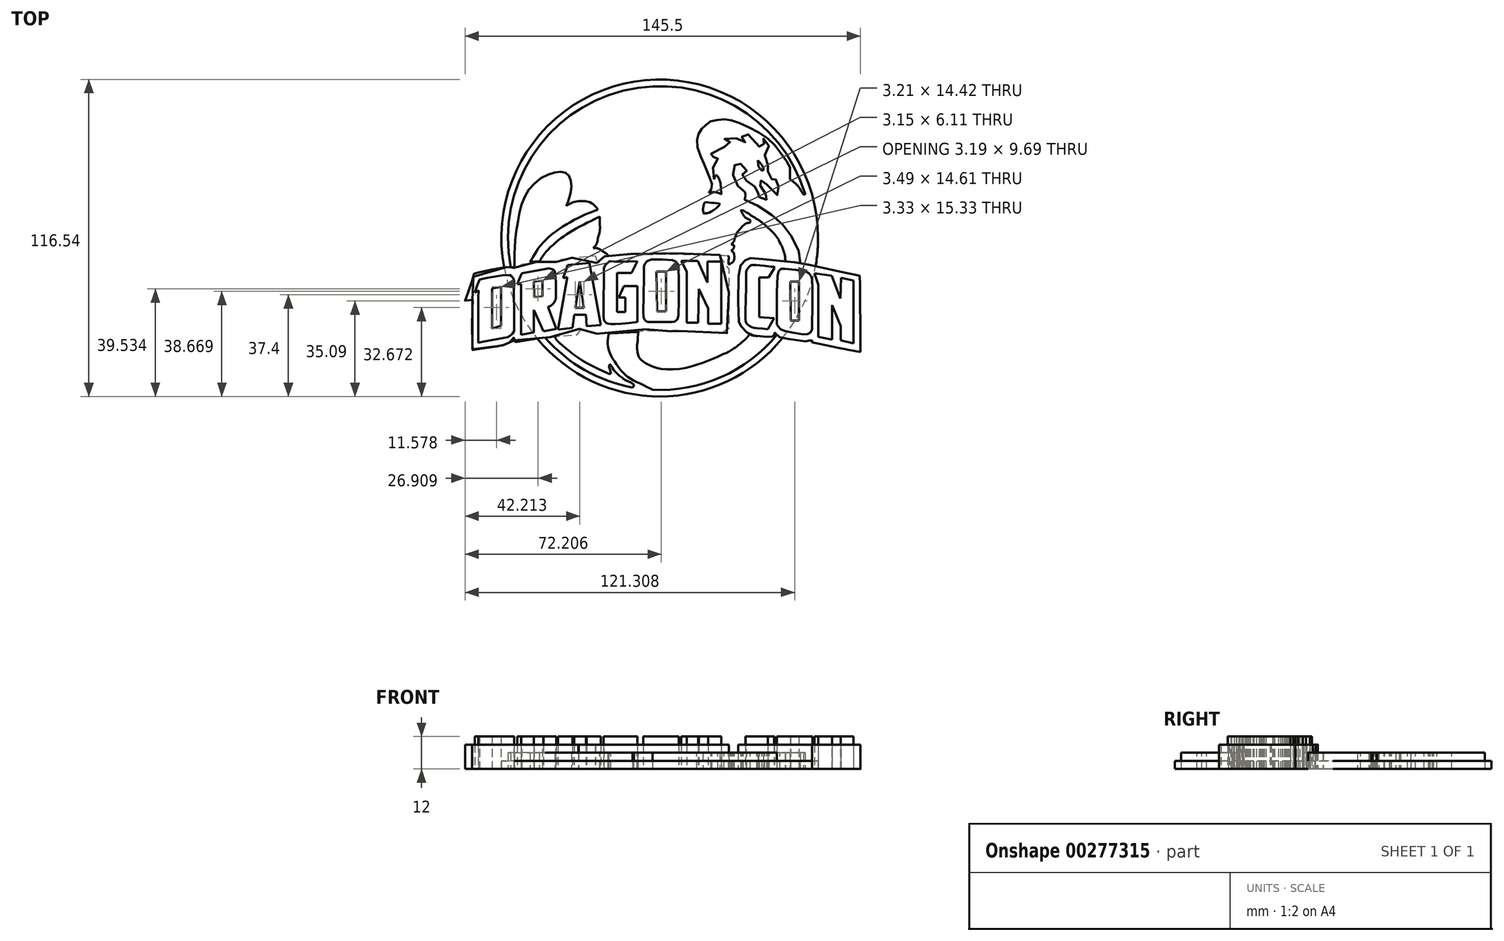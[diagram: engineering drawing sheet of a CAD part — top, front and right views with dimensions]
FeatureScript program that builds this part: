
annotation { "Feature Type Name" : "Feature", "Feature Type Description" : "" }
export const myFeature = defineFeature(function(context is Context, id is Id, definition is map)
    precondition{}
    {
        {
            var Q0;
            Q0=qCreatedBy(makeId("Top.planeOp"),FACE);
            var sketch = newSketch(context, id + "F0", { "sketchPlane" : qUnion([Q0])});
            skCircle(sketch, "E0", {"center": v(-3.25, 16.34) * mm, "radius": 58.27 * mm});
            skCircle(sketch, "E1.0", {"center": v(-3.25, 16.34) * mm, "radius": 55.87 * mm});
            skFitSpline(sketch, "E2", {"points": [v(-50.97, 7.43) * mm, v(-47.94, 12.58) * mm, v(-41.78, 18.63) * mm, v(-32.6, 24.12) * mm, v(-26.1, 26.81) * mm], "startDerivative": vector(12.2, 23.84) * mm, "endDerivative": vector(26.36, 9.93) * mm});
            skFitSpline(sketch, "E3", {"points": [v(-37.64, 28.16) * mm, v(-35.28, 29.5) * mm, v(-32.03, 29.95) * mm, v(-29, 29.5) * mm, v(-26.88, 27.93) * mm, v(-26.1, 26.81) * mm], "startDerivative": vector(10.69, 7.53) * mm, "endDerivative": vector(4.39, -7.37) * mm});
            skFitSpline(sketch, "E4", {"points": [v(-56.8, 5.63) * mm, v(-56.68, 10.34) * mm, v(-56.57, 14.49) * mm, v(-55.45, 22.55) * mm, v(-53.77, 29.61) * mm, v(-50.09, 35.78) * mm, v(-44.47, 39.7) * mm, v(-40.32, 40.7) * mm, v(-37.75, 40.26) * mm, v(-36.3, 38.47) * mm, v(-35.84, 35.78) * mm, v(-36.18, 32.42) * mm, v(-36.96, 30.06) * mm, v(-37.64, 28.16) * mm], "startDerivative": vector(1.87, 60.35) * mm, "endDerivative": vector(-12.09, -35.42) * mm});
            skFitSpline(sketch, "E5", {"points": [v(-25.35, 24.17) * mm, v(-30.1, 21.94) * mm, v(-36.47, 18.42) * mm, v(-40.6, 15.5) * mm, v(-44.44, 12.05) * mm, v(-46.28, 9.75) * mm, v(-47.58, 7.76) * mm], "startDerivative": vector(-25.1, -11.24) * mm, "endDerivative": vector(-10.5, -16.52) * mm});
            skFitSpline(sketch, "E6", {"points": [v(-27.73, 12.67) * mm, v(-26.5, 14.35) * mm, v(-26.04, 16.2) * mm, v(-25.35, 19.1) * mm, v(-25.35, 21.94) * mm, v(-25.35, 24.17) * mm], "startDerivative": vector(7.73, 8.84) * mm, "endDerivative": vector(0.24, 11.19) * mm});
            skFitSpline(sketch, "E7", {"points": [v(-27.73, 12.67) * mm, v(-26.5, 12.67) * mm, v(-24.9, 11.9) * mm, v(-22.6, 10.37) * mm], "startDerivative": vector(4.49, 0.5) * mm, "endDerivative": vector(5.86, -4.02) * mm});
            skFitSpline(sketch, "E8", {"points": [v(19.1, 32.6) * mm, v(17.27, 33.21) * mm, v(14.74, 32.9) * mm], "startDerivative": vector(-3.76, 1.76) * mm, "endDerivative": vector(-4.95, -1.08) * mm});
            skFitSpline(sketch, "E9", {"points": [v(49.54, 32.52) * mm, v(48.62, 33.9) * mm, v(47.62, 35.43) * mm, v(46.32, 36.66) * mm, v(44.63, 37.96) * mm], "startDerivative": vector(-3.93, 5.66) * mm, "endDerivative": vector(-6.46, 4.91) * mm});
            skFitSpline(sketch, "E10", {"points": [v(44.63, 42.4) * mm, v(44.63, 41.03) * mm, v(44.63, 37.96) * mm], "startDerivative": vector(0, -3.1) * mm, "endDerivative": vector(0, -5.62) * mm});
            skFitSpline(sketch, "E11", {"points": [v(44.63, 42.4) * mm, v(43.07, 44.98) * mm, v(39.76, 49.62) * mm, v(35.83, 53.38) * mm, v(29.87, 56.9) * mm, v(24.29, 59.37) * mm, v(21.2, 59.97) * mm, v(18.51, 59.86) * mm, v(15.62, 59.32) * mm, v(14.02, 58.24) * mm, v(12.5, 56.88) * mm, v(11.2, 55.01) * mm, v(10.63, 53.36) * mm, v(10.38, 50.92) * mm, v(12.12, 45.66) * mm, v(13.4, 42.76) * mm, v(14.77, 39.1) * mm, v(15.62, 37.18) * mm, v(15.91, 35) * mm, v(15.29, 33.84) * mm, v(14.74, 32.9) * mm], "startDerivative": vector(-28.1, 47.85) * mm, "endDerivative": vector(-17.14, -31.73) * mm});
            skFitSpline(sketch, "E12", {"points": [v(16.7, 37.9) * mm, v(16.86, 38.65) * mm, v(17.05, 39.17) * mm, v(17.29, 39.37) * mm, v(17.5, 39.43) * mm, v(17.78, 39.35) * mm, v(18.01, 39.03) * mm, v(18.43, 38.29) * mm, v(18.72, 37.72) * mm, v(18.8, 37.47) * mm, v(18.86, 37.1) * mm, v(19.1, 36.26) * mm, v(19.32, 33.08) * mm, v(19.39, 32.6) * mm, v(19.1, 32.6) * mm], "startDerivative": vector(1.88, 9.22) * mm, "endDerivative": vector(-7.19, 1.13) * mm});
            skFitSpline(sketch, "E13", {"points": [v(16.7, 37.9) * mm, v(16.28, 37.9) * mm, v(16.04, 38.79) * mm, v(16.02, 41.8) * mm, v(16.7, 42.73) * mm, v(17.34, 43.42) * mm, v(17.94, 44.76) * mm, v(18.1, 45.34) * mm, v(18.07, 45.8) * mm, v(17.88, 46.28) * mm, v(17.58, 46.58) * mm, v(17.13, 46.6) * mm, v(16.7, 46.5) * mm, v(16.4, 46.18) * mm, v(16.34, 45.57) * mm, v(16, 45.2) * mm, v(15.63, 45.57) * mm, v(15.53, 46.95) * mm, v(15.73, 47.56) * mm, v(18.35, 49.77) * mm, v(18.72, 49.83) * mm, v(21.74, 49.93) * mm, v(22.19, 50.08) * mm, v(22.57, 50.42) * mm, v(22.63, 50.87) * mm, v(22.57, 51.35) * mm, v(22.4, 51.86) * mm, v(21.84, 52.15) * mm, v(20.89, 52.09) * mm, v(20.56, 52.13) * mm, v(20.4, 52.43) * mm, v(20.62, 52.88) * mm, v(21.64, 53.14) * mm, v(23.35, 53.34) * mm, v(24.62, 53.16) * mm, v(25.33, 52.63) * mm, v(26.19, 51.92) * mm, v(27.39, 51.54) * mm, v(28.2, 51.66) * mm, v(28.58, 52.27) * mm, v(28.52, 53.1) * mm, v(28.01, 53.45) * mm, v(27.02, 53.45) * mm, v(26.76, 53.65) * mm, v(26.8, 54) * mm, v(27.06, 54.32) * mm, v(27.77, 54.52) * mm, v(29.11, 54.48) * mm, v(29.84, 54.26) * mm, v(32.75, 50.58) * mm, v(33.3, 50) * mm, v(33.76, 49.9) * mm, v(34.09, 49.91) * mm, v(34.47, 50.01) * mm, v(34.8, 50.26) * mm, v(35.06, 50.58) * mm, v(35.08, 51) * mm, v(35, 51.42) * mm, v(34.63, 51.66) * mm, v(34.37, 51.98) * mm, v(34.29, 52.33) * mm, v(34.37, 52.71) * mm, v(34.84, 52.88) * mm, v(35.4, 52.65) * mm, v(36.01, 52.1) * mm, v(36.32, 51.62) * mm, v(36.7, 50.93) * mm, v(36.77, 49.04) * mm, v(36.48, 48.35) * mm, v(36.08, 47.64) * mm, v(35.38, 46.97) * mm, v(35.34, 46.75) * mm, v(35.36, 46.26) * mm, v(35.34, 45.22) * mm, v(35.87, 44.15) * mm, v(36.8, 42.77) * mm, v(36.93, 42.38) * mm, v(36.85, 41.77) * mm, v(36.56, 41.6) * mm, v(36.48, 41.3) * mm, v(36.44, 40.92) * mm, v(36.48, 40.37) * mm, v(36.48, 39.84) * mm, v(36.79, 39.3) * mm, v(37.35, 38.64) * mm, v(38.09, 37.75) * mm, v(38.51, 37.28) * mm, v(38.73, 37.18) * mm, v(39.06, 37.22) * mm, v(39.16, 37.37) * mm, v(39.2, 37.59) * mm, v(39.26, 37.73) * mm, v(39.55, 37.9) * mm, v(39.8, 37.71) * mm, v(39.91, 37.26) * mm, v(40.16, 35.82) * mm, v(40.28, 35.11) * mm, v(40.52, 35.42) * mm, v(40.95, 31.01) * mm, v(40.85, 30.97) * mm, v(39.06, 33.35) * mm, v(37.31, 35.07) * mm, v(36.12, 36.05) * mm, v(36.1, 36.07) * mm, v(36.12, 36.07) * mm, v(36.48, 36.35) * mm], "startDerivative": vector(-64.1, -13.42) * mm, "endDerivative": vector(60.5, 53.27) * mm});
            skFitSpline(sketch, "E14", {"points": [v(36.12, 36.07) * mm, v(35.12, 37.15) * mm, v(34.57, 37.47) * mm, v(34.18, 37.57) * mm, v(33.81, 37.46) * mm, v(33.6, 37.13) * mm, v(33.5, 36.78) * mm, v(33.53, 36.18) * mm, v(33.72, 35.5) * mm, v(34.37, 34.3) * mm, v(35.57, 32.65) * mm, v(36.12, 31.8) * mm, v(36.26, 30.98) * mm, v(36.22, 30.43) * mm, v(35.73, 30.61) * mm, v(34.7, 31.2) * mm, v(33.99, 31.42) * mm, v(32.9, 31.45) * mm, v(32.44, 31.7) * mm, v(32.63, 32.04) * mm, v(32.87, 32.46) * mm, v(32.96, 32.86) * mm, v(32.91, 33.13) * mm, v(32.7, 33.78) * mm, v(32.03, 34.83) * mm, v(31.1, 35.85) * mm, v(29.88, 36.62) * mm, v(28.5, 37.5) * mm, v(27.5, 38.23) * mm, v(27.08, 38.9) * mm, v(27.11, 39.74) * mm, v(27.57, 40.34) * mm, v(28.4, 40.66) * mm, v(28.63, 40.75) * mm, v(28.66, 41.17) * mm, v(28.4, 41.74) * mm, v(26.94, 43.34) * mm, v(26.27, 43.7) * mm, v(25.45, 43.76) * mm, v(24.66, 43.62) * mm, v(24.34, 43.27) * mm, v(23.87, 42.1) * mm, v(23.7, 40.75) * mm, v(23.8, 39.02) * mm, v(24.66, 36.86) * mm, v(25.92, 34.99) * mm, v(27.23, 33.75) * mm, v(27.88, 33.28) * mm, v(28.47, 33.04) * mm, v(28.78, 32.38) * mm, v(28.66, 31.99) * mm, v(28.3, 31.88) * mm, v(27.97, 32.28) * mm, v(27.44, 31.94) * mm, v(27.52, 30.77) * mm, v(27.96, 30.48) * mm, v(30.2, 29.65) * mm, v(33.98, 27.55) * mm, v(37.62, 25.05) * mm, v(40.25, 22.92) * mm, v(42.51, 20.58) * mm, v(44.37, 18.12) * mm, v(45.9, 15.85) * mm, v(47.92, 11.49) * mm, v(48.4, 8.13) * mm, v(48.36, 7.2) * mm], "startDerivative": vector(-57.86, 70.9) * mm, "endDerivative": vector(-4.92, -56.1) * mm});
            skFitSpline(sketch, "E15", {"points": [v(13.27, 29.46) * mm, v(12.95, 28.76) * mm, v(12.7, 27.87) * mm, v(12.62, 26.9) * mm, v(12.66, 26.06) * mm, v(12.9, 25.4) * mm, v(13.04, 25.35) * mm, v(13.53, 25.43) * mm, v(14.79, 25.7) * mm, v(16.58, 26.68) * mm, v(18.8, 28.76) * mm, v(18.74, 29) * mm, v(16.54, 29.26) * mm, v(14.72, 29.42) * mm, v(13.27, 29.46) * mm]});
            skFitSpline(sketch, "E16", {"points": [v(26.9, 26.8) * mm, v(28.62, 25.8) * mm, v(30.72, 24.44) * mm, v(33.66, 22.55) * mm, v(36.65, 20.04) * mm, v(38.21, 18.56) * mm, v(38.95, 17.71) * mm, v(40.1, 16.25) * mm, v(40.7, 15.15) * mm, v(41.43, 13.7) * mm, v(41.82, 12.95) * mm, v(42.23, 11.73) * mm, v(42.69, 10.09) * mm, v(42.92, 8.04) * mm], "startDerivative": vector(21.56, -12.1) * mm, "endDerivative": vector(1.9, -26.3) * mm});
            skFitSpline(sketch, "E17", {"points": [v(26.83, 26.8) * mm, v(26.62, 26.7) * mm, v(26.85, 25.9) * mm, v(27.63, 24.56) * mm, v(28.04, 24.07) * mm, v(28.83, 23.49) * mm, v(29.65, 23.14) * mm, v(29.95, 22.88) * mm, v(30, 22.5) * mm, v(29.95, 22.1) * mm, v(29.16, 21.92) * mm, v(28.38, 21.72) * mm, v(27.52, 21.01) * mm, v(26.64, 20.2) * mm, v(25.78, 19.14) * mm, v(25.3, 18.58) * mm, v(24.77, 17.5) * mm, v(24.3, 16.2) * mm, v(24.06, 15.38) * mm, v(23.52, 14.54) * mm, v(23.15, 14.13) * mm, v(23.33, 13.9) * mm, v(23.67, 13.85) * mm, v(24, 13.66) * mm, v(24.06, 13.14) * mm, v(23.82, 12.47) * mm, v(23.28, 12.04) * mm, v(23.18, 11.5) * mm, v(23.76, 11.2) * mm, v(24.1, 9.87) * mm, v(24.06, 8.45) * mm, v(23.9, 7.91) * mm, v(23.71, 7.63) * mm, v(22.79, 6.97) * mm, v(22.34, 6.77) * mm], "startDerivative": vector(-16.2, -3.25) * mm, "endDerivative": vector(-16.34, -5.45) * mm});
            skFitSpline(sketch, "E18", {"points": [v(-40.23, -22.15) * mm, v(-38.16, -23.95) * mm, v(-35.75, -25.9) * mm, v(-32.9, -27.94) * mm, v(-29.2, -30.12) * mm, v(-24.86, -32.23) * mm, v(-22.72, -33.26) * mm, v(-21.49, -33.68) * mm, v(-21.3, -33.5) * mm, v(-21.34, -33.19) * mm, v(-21.49, -32.69) * mm, v(-21.68, -31.77) * mm, v(-21.83, -31.39) * mm, v(-21.91, -30.24) * mm, v(-21.57, -30.16) * mm, v(-21.18, -30.5) * mm, v(-20.76, -31.35) * mm, v(-20, -32.42) * mm, v(-18.88, -33.65) * mm, v(-17.04, -35.1) * mm], "startDerivative": vector(28.15, -24.84) * mm, "endDerivative": vector(29.6, -21.78) * mm});
            skFitSpline(sketch, "E19", {"points": [v(-17.04, -35.1) * mm, v(-15.55, -36.1) * mm, v(-13.75, -36.9) * mm, v(-12.9, -37.48) * mm, v(-12.79, -37.86) * mm, v(-13.33, -38.6) * mm], "startDerivative": vector(5.46, -4.1) * mm, "endDerivative": vector(-4.14, -3) * mm});
            skFitSpline(sketch, "E20", {"points": [v(32.76, 44.92) * mm, v(33.4, 44.27) * mm, v(34.36, 43.1) * mm, v(34.8, 42.23) * mm, v(34.8, 42.1) * mm, v(34.8, 41.34) * mm, v(34.66, 41.25) * mm, v(34.43, 41.23) * mm, v(34.14, 41.3) * mm, v(33.04, 42.68) * mm, v(33.02, 42.91) * mm, v(32.76, 44.92) * mm]});
            skFitSpline(sketch, "E21", {"points": [v(-11.42, -20.07) * mm, v(-11.47, -21.62) * mm, v(-11.68, -23.04) * mm, v(-11.64, -23.98) * mm, v(-11.52, -25.28) * mm, v(-11.28, -26.4) * mm, v(-11.12, -27.03) * mm, v(-10.98, -27.36) * mm, v(-10.6, -28) * mm, v(-10.03, -28.59) * mm, v(-9.33, -29.13) * mm, v(-8.28, -29.78) * mm, v(-6.81, -30.56) * mm, v(-5.08, -31.25) * mm, v(-3.09, -31.74) * mm, v(-0.2, -31.95) * mm, v(4, -31.77) * mm, v(7.46, -31.09) * mm, v(10.42, -30.2) * mm, v(15.41, -28.43) * mm, v(20, -26.37) * mm], "startDerivative": vector(0.6, -33.32) * mm, "endDerivative": vector(52.9, 25.28) * mm});
            skFitSpline(sketch, "E22", {"points": [v(20, -26.37) * mm, v(22.61, -25.17) * mm, v(25.76, -22.93) * mm, v(28.22, -20.87) * mm], "startDerivative": vector(8.27, 3.24) * mm, "endDerivative": vector(7.15, 6.13) * mm});
            skFitSpline(sketch, "E23", {"points": [v(-22.32, -20.3) * mm, v(-22.38, -23.47) * mm, v(-21.42, -26.48) * mm, v(-19.58, -29.61) * mm, v(-17.77, -32.06) * mm, v(-16.05, -33.9) * mm, v(-13.52, -35.7) * mm, v(-9.27, -37.72) * mm, v(-5.94, -39.46) * mm], "startDerivative": vector(-2.32, -26.36) * mm, "endDerivative": vector(24.45, -10.25) * mm});
            skFitSpline(sketch, "E24", {"points": [v(-69.99, -3.2) * mm, v(-69.95, -22.17) * mm], "startDerivative": vector(0.04, -18.97) * mm, "endDerivative": vector(0.04, -18.97) * mm});
            skFitSpline(sketch, "E25", {"points": [v(-69.95, -22.17) * mm, v(-59.54, -20.12) * mm, v(-58.9, -19.93) * mm, v(-58.38, -19.6) * mm, v(-57.8, -19.15) * mm, v(-57.22, -18.41) * mm, v(-56.87, -17.67) * mm, v(-56.87, -15.7) * mm, v(-56.95, 0.96) * mm, v(-57.15, 1.64) * mm, v(-57.48, 2) * mm, v(-58.14, 2.54) * mm, v(-58.59, 2.83) * mm, v(-58.77, 2.85) * mm, v(-69.3, 1.14) * mm, v(-69.43, 1.1) * mm, v(-71.42, -3.5) * mm, v(-71.32, -3.64) * mm, v(-71, -3.64) * mm, v(-69.99, -3.2) * mm], "startDerivative": vector(102.59, 19.96) * mm, "endDerivative": vector(26.52, 13.63) * mm});
            skFitSpline(sketch, "E26", {"points": [v(-65, -2.3) * mm, v(-65.03, -16.9) * mm], "startDerivative": vector(-0.04, -14.6) * mm, "endDerivative": vector(-0.04, -14.6) * mm});
            skFitSpline(sketch, "E27", {"points": [v(-61.77, -1.6) * mm, v(-65, -2.3) * mm], "startDerivative": vector(-3.22, -0.69) * mm, "endDerivative": vector(-3.22, -0.69) * mm});
            skFitSpline(sketch, "E28", {"points": [v(-61.83, -15.89) * mm, v(-61.77, -1.6) * mm], "startDerivative": vector(0.05, 14.28) * mm, "endDerivative": vector(0.05, 14.28) * mm});
            skFitSpline(sketch, "E29", {"points": [v(-65.03, -16.9) * mm, v(-61.83, -15.89) * mm], "startDerivative": vector(3.2, 1.01) * mm, "endDerivative": vector(3.2, 1.01) * mm});
            skFitSpline(sketch, "E30", {"points": [v(-46.45, 0.98) * mm, v(-49.44, 0.67) * mm], "startDerivative": vector(-3, -0.3) * mm, "endDerivative": vector(-3, -0.3) * mm});
            skFitSpline(sketch, "E31", {"points": [v(-46.3, -5.24) * mm, v(-46.45, 0.98) * mm], "startDerivative": vector(-0.14, 6.21) * mm, "endDerivative": vector(-0.14, 6.21) * mm});
            skFitSpline(sketch, "E32", {"points": [v(-49.52, -5.5) * mm, v(-46.3, -5.24) * mm], "startDerivative": vector(3.22, 0.26) * mm, "endDerivative": vector(3.22, 0.26) * mm});
            skFitSpline(sketch, "E33", {"points": [v(-49.44, 0.67) * mm, v(-49.52, -5.5) * mm], "startDerivative": vector(-0.08, -6.17) * mm, "endDerivative": vector(-0.08, -6.17) * mm});
            skFitSpline(sketch, "E34", {"points": [v(-22.6, 10.37) * mm, v(-22.15, 9.89) * mm, v(-20.92, 9.98) * mm, v(11.44, 10.37) * mm, v(21.6, 9.89) * mm], "startDerivative": vector(5.82, -7.96) * mm, "endDerivative": vector(24.52, -1.9) * mm});
            skFitSpline(sketch, "E35", {"points": [v(22.34, 6.77) * mm, v(22, 6.77) * mm, v(22.03, 9.66) * mm, v(21.6, 9.89) * mm], "startDerivative": vector(-2.05, -0.95) * mm, "endDerivative": vector(-2.24, -0.03) * mm});
            skFitSpline(sketch, "E36", {"points": [v(-50.97, 7.43) * mm, v(-49.6, 7.64) * mm, v(-47.58, 7.76) * mm], "startDerivative": vector(2.87, 0.5) * mm, "endDerivative": vector(3.87, 0.17) * mm});
            skFitSpline(sketch, "E37", {"points": [v(-56.8, 5.63) * mm, v(-56.8, 5.3) * mm], "startDerivative": vector(0, -0.34) * mm, "endDerivative": vector(0, -0.34) * mm});
            skFitSpline(sketch, "E38", {"points": [v(-56.8, 5.3) * mm, v(-57.15, 5.47) * mm, v(-57.59, 5.63) * mm, v(-58.08, 5.66) * mm], "startDerivative": vector(-1.09, 0.57) * mm, "endDerivative": vector(-1.42, 0.01) * mm});
            skFitSpline(sketch, "E39", {"points": [v(49.54, 32.52) * mm, v(49.83, 32.32) * mm, v(50.2, 32.6) * mm], "startDerivative": vector(0.62, -0.63) * mm, "endDerivative": vector(0.63, 0.75) * mm});
            skFitSpline(sketch, "E40", {"points": [v(42.92, 8.04) * mm, v(42.92, 7.69) * mm, v(43.04, 7.69) * mm, v(45.94, 7.43) * mm, v(48.35, 7.07) * mm, v(48.36, 7.07) * mm, v(48.36, 7.2) * mm], "startDerivative": vector(-0.35, -3.72) * mm, "endDerivative": vector(-0.1, 2.41) * mm});
            skFitSpline(sketch, "E41", {"points": [v(-56.8, 5.3) * mm, v(-56.33, 5.3) * mm, v(-56.12, 6.27) * mm, v(-55.26, 6.54) * mm, v(-50.97, 7.43) * mm], "startDerivative": vector(3.85, -1.21) * mm, "endDerivative": vector(11.27, 2.66) * mm});
            skFitSpline(sketch, "E42", {"points": [v(-47.58, 7.76) * mm, v(-45.09, 7.96) * mm, v(-43.55, 8.04) * mm, v(-42.59, 8.01) * mm, v(-41.8, 7.88) * mm, v(-41.22, 7.52) * mm, v(-40.23, 6.59) * mm, v(-39.98, 6.36) * mm, v(-39.94, 6.37) * mm, v(-39.04, 8.7) * mm, v(-38.98, 8.77) * mm, v(-26.98, 9.8) * mm, v(-26.98, 9.78) * mm, v(-26.55, 7.35) * mm, v(-26.36, 6.71) * mm, v(-26.2, 6.71) * mm, v(-25.77, 7.5) * mm, v(-25.11, 8.42) * mm, v(-24.31, 9.17) * mm, v(-23.42, 9.8) * mm, v(-22.6, 10.37) * mm], "startDerivative": vector(34.56, 2.98) * mm, "endDerivative": vector(17.1, 11.49) * mm});
            skFitSpline(sketch, "E43", {"points": [v(48.36, 7.07) * mm, v(49.74, 6.82) * mm, v(51.72, 6.34) * mm], "startDerivative": vector(2.9, -0.46) * mm, "endDerivative": vector(3.76, -0.96) * mm});
            skFitSpline(sketch, "E44", {"points": [v(22.2, 6.71) * mm, v(22.2, -17.98) * mm, v(22.2, -18.17) * mm, v(21.95, -18.45) * mm, v(21.05, -18.54) * mm, v(4.01, -17.8) * mm, v(3.69, -17.76) * mm, v(3.64, -17.6) * mm, v(3.64, -16.86) * mm, v(3.56, -16.9) * mm, v(3.3, -17.13) * mm, v(2.87, -17.5) * mm, v(2.32, -17.7) * mm, v(1.77, -17.9) * mm, v(0.3, -17.9) * mm, v(-7.27, -17.88) * mm, v(-7.61, -17.7) * mm, v(-8.37, -17.09) * mm, v(-8.48, -17.3) * mm, v(-8.75, -17.8) * mm, v(-8.94, -17.9) * mm, v(-32.16, -19.1) * mm, v(-32.38, -18.95) * mm, v(-32.73, -16.45) * mm, v(-33.22, -19.08) * mm, v(-33.43, -19.19) * mm, v(-37.87, -19.52) * mm, v(-45.42, -20.3) * mm], "startDerivative": vector(-1.58, -264.35) * mm, "endDerivative": vector(-101.85, -10.87) * mm});
            skFitSpline(sketch, "E45", {"points": [v(42.92, 7.69) * mm, v(41.83, 7.89) * mm, v(39.32, 8.26) * mm, v(36.49, 8.63) * mm, v(32.1, 9.18) * mm, v(29.87, 9.29) * mm, v(28.6, 8.84) * mm, v(27.32, 7.97) * mm, v(26.11, 6.42) * mm, v(25.76, 5.79) * mm, v(25.58, 4.23) * mm, v(25.51, -13.86) * mm, v(25.51, -14.02) * mm, v(25.73, -14.8) * mm, v(26.25, -15.96) * mm, v(26.84, -17.02) * mm, v(28.11, -18.15) * mm, v(29.34, -18.9) * mm, v(30.75, -19.43) * mm, v(33.1, -19.75) * mm, v(35.03, -19.87) * mm, v(38, -20.03) * mm, v(38.15, -19.93) * mm, v(38.92, -18.6) * mm, v(39.06, -18.52) * mm, v(39.8, -19.27) * mm], "startDerivative": vector(-30.28, 5.9) * mm, "endDerivative": vector(28.9, -33.22) * mm});
            skFitSpline(sketch, "E46", {"points": [v(-11.42, -20.07) * mm, v(-11.14, -18.1) * mm], "startDerivative": vector(0.28, 1.98) * mm, "endDerivative": vector(0.28, 1.98) * mm});
            skFitSpline(sketch, "E47", {"points": [v(-22.32, -20.3) * mm, v(-22.1, -18.67) * mm], "startDerivative": vector(0.2, 1.64) * mm, "endDerivative": vector(0.2, 1.64) * mm});
            skFitSpline(sketch, "E48", {"points": [v(28.22, -20.87) * mm, v(29.14, -19.84) * mm, v(29.67, -19.06) * mm], "startDerivative": vector(1.82, 1.91) * mm, "endDerivative": vector(1.06, 1.7) * mm});
            skFitSpline(sketch, "E49", {"points": [v(-40.23, -22.15) * mm, v(-41.3, -21.05) * mm, v(-41.84, -19.92) * mm], "startDerivative": vector(-2.25, 2.02) * mm, "endDerivative": vector(-0.94, 2.42) * mm});
            skFitSpline(sketch, "E50", {"points": [v(-58.08, 5.66) * mm, v(-59.65, 5.66) * mm, v(-71.13, 3.5) * mm, v(-71.38, 3.32) * mm, v(-74.85, -6.53) * mm, v(-74.85, -6.6) * mm], "startDerivative": vector(-6.16, 1.27) * mm, "endDerivative": vector(0.58, -0.62) * mm});
            skFitSpline(sketch, "E51", {"points": [v(-74.85, -6.6) * mm, v(-72.57, -6.6) * mm, v(-72.18, -6.6) * mm, v(-72.14, -24.78) * mm, v(-71.96, -24.56) * mm, v(-59.5, -22.54) * mm, v(-56.95, -20.3) * mm, v(-56.6, -22) * mm, v(-56.43, -22) * mm, v(-45.42, -20.3) * mm], "startDerivative": vector(31.5, -3.14) * mm, "endDerivative": vector(79.56, 10.88) * mm});
            skFitSpline(sketch, "E52", {"points": [v(39.8, -19.27) * mm, v(40.81, -20.05) * mm, v(42.3, -20.55) * mm, v(49.13, -21.54) * mm, v(51.67, -21.6) * mm, v(52.82, -20.83) * mm, v(52.8, -20.96) * mm, v(52.7, -22.02) * mm, v(52.77, -22.06) * mm, v(70.3, -25.46) * mm, v(70.32, -25.3) * mm, v(70.4, 2.66) * mm, v(70.23, 2.66) * mm, v(62.93, 4.17) * mm, v(54.83, 5.66) * mm, v(51.72, 6.34) * mm], "startDerivative": vector(24.44, -20.7) * mm, "endDerivative": vector(-42.53, 10.23) * mm});
            skLineSegment(sketch, "E53", {"start": v(23.71, 7.63) * mm, "end": v(26.11, 6.42) * mm});
            skLineSegment(sketch, "E54", {"start": v(32.1, 9.18) * mm, "end": v(24.77, 17.5) * mm});
            skLineSegment(sketch, "E55", {"start": v(36.65, 20.04) * mm, "end": v(28.43, 13.34) * mm});
            skLineSegment(sketch, "E56", {"start": v(33.66, 22.55) * mm, "end": v(26.64, 20.2) * mm});
            skLineSegment(sketch, "E57", {"start": v(28.62, 25.8) * mm, "end": v(27.63, 24.56) * mm});
            skLineSegment(sketch, "E58", {"start": v(27.47, 26.48) * mm, "end": v(26.62, 26.7) * mm});
            skLineSegment(sketch, "E59", {"start": v(22.16, -1.95) * mm, "end": v(25.53, -10.16) * mm});
            skLineSegment(sketch, "E60", {"start": v(25.54, 0.72) * mm, "end": v(22.19, 3.59) * mm});
            skLineSegment(sketch, "E61", {"start": v(22.34, 6.77) * mm, "end": v(22.19, 3.59) * mm});
            skSolve(sketch);
        }
        {
            var Q0;
            Q0=qCreatedBy(makeId("Top.planeOp"),FACE);
            var sketch = newSketch(context, id + "F1", { "sketchPlane" : qUnion([Q0])});
            skFitSpline(sketch, "E62", {"points": [v(-59.64, 5.71) * mm, v(-59.48, 5.67) * mm, v(-58.49, 5.67) * mm, v(-57.61, 5.56) * mm, v(-56.9, 5.29) * mm, v(-56.6, 5.12) * mm, v(-56.46, 5.14) * mm, v(-56.1, 6.16) * mm, v(-55.88, 6.33) * mm, v(-50.98, 7.3) * mm, v(-47.58, 7.69) * mm, v(-43.3, 8.01) * mm, v(-42.15, 7.92) * mm, v(-41.26, 7.53) * mm, v(-40, 6.37) * mm, v(-39.95, 6.38) * mm, v(-38.97, 8.7) * mm, v(-38.91, 8.76) * mm, v(-27.02, 9.8) * mm, v(-27.05, 9.73) * mm, v(-26.95, 9.73) * mm, v(-26.95, 9.52) * mm, v(-26.4, 6.7) * mm, v(-26.28, 6.67) * mm, v(-25.73, 7.53) * mm, v(-25.16, 8.42) * mm, v(-24.32, 9.16) * mm, v(-23.33, 9.8) * mm, v(-22.35, 10.16) * mm, v(-20.56, 10.34) * mm, v(-6.7, 10.71) * mm, v(3.3, 10.77) * mm, v(16.38, 10.32) * mm, v(21.82, 9.93) * mm, v(21.95, 9.8) * mm, v(22.16, -17.92) * mm, v(22.16, -18.24) * mm, v(21.98, -18.38) * mm, v(21.47, -18.6) * mm, v(21.03, -18.56) * mm, v(3.95, -17.85) * mm, v(3.7, -17.7) * mm, v(3.63, -16.88) * mm, v(3.5, -16.97) * mm, v(3.05, -17.3) * mm, v(2.62, -17.6) * mm, v(1.53, -17.94) * mm, v(-7.33, -17.9) * mm, v(-7.5, -17.89) * mm, v(-8.21, -17.14) * mm, v(-8.37, -17.14) * mm, v(-8.82, -17.85) * mm, v(-9.17, -17.96) * mm, v(-32.17, -19.16) * mm, v(-32.26, -19.14) * mm, v(-32.36, -18.97) * mm, v(-32.65, -16.45) * mm, v(-32.7, -16.45) * mm, v(-33.2, -19.07) * mm, v(-33.16, -19.18) * mm, v(-45.48, -20.35) * mm, v(-56.54, -21.99) * mm, v(-56.64, -21.99) * mm, v(-56.94, -20.25) * mm, v(-57.15, -20.38) * mm, v(-58, -21.4) * mm, v(-59.4, -22.56) * mm, v(-65.95, -23.84) * mm, v(-72.1, -24.81) * mm, v(-72.18, -24.73) * mm, v(-72.16, -6.55) * mm, v(-72.2, -6.36) * mm, v(-74.91, -6.74) * mm, v(-74.91, -6.63) * mm, v(-71.6, 3.06) * mm, v(-71.2, 3.43) * mm, v(-59.64, 5.71) * mm]});
            skFitSpline(sketch, "E63", {"points": [v(70.28, 2.54) * mm, v(57.5, 5.17) * mm, v(48.41, 7.1) * mm, v(40.25, 8.02) * mm, v(30.86, 9) * mm, v(29.15, 8.83) * mm, v(28.07, 8.1) * mm, v(26.6, 6.58) * mm, v(25.87, 4.41) * mm, v(25.87, -14.39) * mm, v(26.08, -15.04) * mm, v(26.76, -16.29) * mm, v(28.66, -18.27) * mm, v(29.8, -19.14) * mm, v(35.69, -19.98) * mm, v(38.1, -20.03) * mm, v(38.21, -19.95) * mm, v(39.03, -18.46) * mm, v(39.16, -18.51) * mm, v(39.95, -19.27) * mm, v(40.9, -20.11) * mm, v(41.98, -20.47) * mm, v(51.02, -21.74) * mm, v(51.7, -21.66) * mm, v(52.8, -20.93) * mm, v(52.78, -21) * mm, v(52.7, -22.07) * mm], "startDerivative": vector(-156.83, 32.72) * mm, "endDerivative": vector(-0.8, -54.61) * mm});
            skFitSpline(sketch, "E64", {"points": [v(52.7, -22.07) * mm, v(70.36, -25.5) * mm, v(70.44, -25.47) * mm, v(70.28, 2.54) * mm], "startDerivative": vector(58.8, -11.7) * mm, "endDerivative": vector(-1.12, 75.93) * mm});
            skSolve(sketch);
        }
        {
            var Q0;
            Q0=qCreatedBy(makeId("Top.planeOp"),FACE);
            var sketch = newSketch(context, id + "F2", { "sketchPlane" : qUnion([Q0])});
            skFitSpline(sketch, "E65", {"points": [v(-71.32, -3.67) * mm, v(-69.52, 1.01) * mm, v(-69.5, 1.09) * mm, v(-58.69, 2.85) * mm, v(-58.38, 2.7) * mm, v(-58.13, 2.6) * mm, v(-57.54, 2.08) * mm, v(-56.99, 1.4) * mm, v(-56.93, 0) * mm, v(-56.83, -17.47) * mm, v(-56.93, -17.9) * mm, v(-57.42, -18.61) * mm, v(-58.03, -19.3) * mm, v(-58.84, -19.91) * mm, v(-59.6, -20.09) * mm, v(-69.95, -22.13) * mm, v(-70.05, -22.02) * mm, v(-69.95, -3.14) * mm, v(-69.98, -2.98) * mm, v(-71.32, -3.67) * mm]});
            skLineSegment(sketch, "E66", {"start": v(-64.97, -2.23) * mm, "end": v(-61.7, -1.56) * mm});
            skLineSegment(sketch, "E67", {"start": v(-61.7, -1.56) * mm, "end": v(-61.7, -15.88) * mm});
            skLineSegment(sketch, "E68", {"start": v(-61.7, -15.88) * mm, "end": v(-65.04, -16.9) * mm});
            skLineSegment(sketch, "E69", {"start": v(-65.04, -16.9) * mm, "end": v(-64.97, -2.23) * mm});
            skLineSegment(sketch, "E70", {"start": v(-49.62, 0.34) * mm, "end": v(-46.47, 0.7) * mm});
            skLineSegment(sketch, "E71", {"start": v(-46.47, 0.7) * mm, "end": v(-46.47, -5.15) * mm});
            skLineSegment(sketch, "E72", {"start": v(-46.47, -5.15) * mm, "end": v(-49.5, -5.42) * mm});
            skLineSegment(sketch, "E73", {"start": v(-49.5, -5.42) * mm, "end": v(-49.62, 0.34) * mm});
            skLineSegment(sketch, "E74", {"start": v(-32.8, 0.34) * mm, "end": v(-34.33, -9.35) * mm});
            skLineSegment(sketch, "E75", {"start": v(-34.33, -9.35) * mm, "end": v(-31.14, -9.35) * mm});
            skLineSegment(sketch, "E76", {"start": v(-31.14, -9.35) * mm, "end": v(-32.8, 0.34) * mm});
            skLineSegment(sketch, "E77", {"start": v(-15.94, -5.5) * mm, "end": v(-15.94, -10.85) * mm});
            skLineSegment(sketch, "E78", {"start": v(-15.94, -10.85) * mm, "end": v(-19, -10.85) * mm});
            skLineSegment(sketch, "E79", {"start": v(-19, -10.85) * mm, "end": v(-19, 3.46) * mm});
            skLineSegment(sketch, "E80", {"start": v(-19, 3.46) * mm, "end": v(-13.7, 3.46) * mm});
            skLineSegment(sketch, "E81", {"start": v(-16.51, -1.35) * mm, "end": v(-11.48, -1.35) * mm});
            skLineSegment(sketch, "E82", {"start": v(-11.48, -1.35) * mm, "end": v(-11.48, -14.54) * mm});
            skLineSegment(sketch, "E83", {"start": v(-16.51, -1.35) * mm, "end": v(-18.35, -5.54) * mm});
            skLineSegment(sketch, "E84", {"start": v(-18.35, -5.54) * mm, "end": v(-15.94, -5.5) * mm});
            skLineSegment(sketch, "E85", {"start": v(-4.5, 4.07) * mm, "end": v(-1, 4.07) * mm});
            skLineSegment(sketch, "E86", {"start": v(-1, 4.07) * mm, "end": v(-1, -10.54) * mm});
            skLineSegment(sketch, "E87", {"start": v(-1, -10.54) * mm, "end": v(-4.3, -10.54) * mm});
            skLineSegment(sketch, "E88", {"start": v(-4.3, -10.54) * mm, "end": v(-4.5, 4.07) * mm});
            skLineSegment(sketch, "E89", {"start": v(10.77, -14.8) * mm, "end": v(6.6, -14.8) * mm});
            skLineSegment(sketch, "E90", {"start": v(6.6, -14.8) * mm, "end": v(6.6, 4.07) * mm});
            skLineSegment(sketch, "E91", {"start": v(6.6, 4.07) * mm, "end": v(4.54, 7.96) * mm});
            skLineSegment(sketch, "E92", {"start": v(4.54, 7.96) * mm, "end": v(10.73, 7.96) * mm});
            skLineSegment(sketch, "E93", {"start": v(10.73, 7.96) * mm, "end": v(14.3, 0) * mm});
            skLineSegment(sketch, "E94", {"start": v(14.3, 0) * mm, "end": v(14.3, 7.77) * mm});
            skLineSegment(sketch, "E95", {"start": v(14.3, 7.77) * mm, "end": v(19.32, 7.77) * mm});
            skLineSegment(sketch, "E96", {"start": v(19.32, 7.77) * mm, "end": v(19.32, -15.18) * mm});
            skLineSegment(sketch, "E97", {"start": v(19.32, -15.18) * mm, "end": v(14.46, -15.18) * mm});
            skLineSegment(sketch, "E98", {"start": v(14.46, -15.18) * mm, "end": v(14.46, -9.58) * mm});
            skLineSegment(sketch, "E99", {"start": v(14.46, -9.58) * mm, "end": v(11.11, -2.32) * mm});
            skLineSegment(sketch, "E100", {"start": v(11.11, -2.32) * mm, "end": v(10.77, -14.8) * mm});
            skLineSegment(sketch, "E101", {"start": v(38.87, 5.34) * mm, "end": v(36.74, 1.81) * mm});
            skLineSegment(sketch, "E102", {"start": v(36.74, 1.81) * mm, "end": v(33.36, 1.81) * mm});
            skLineSegment(sketch, "E103", {"start": v(33.36, 1.81) * mm, "end": v(33.36, -12.79) * mm});
            skLineSegment(sketch, "E104", {"start": v(33.36, -12.79) * mm, "end": v(38.77, -13.1) * mm});
            skLineSegment(sketch, "E105", {"start": v(38.77, -13.1) * mm, "end": v(36.47, -17.13) * mm});
            skLineSegment(sketch, "E106", {"start": v(44.75, 0.4) * mm, "end": v(47.97, 0.4) * mm});
            skLineSegment(sketch, "E107", {"start": v(47.97, 0.4) * mm, "end": v(47.97, -14.02) * mm});
            skLineSegment(sketch, "E108", {"start": v(47.97, -14.02) * mm, "end": v(44.87, -14.02) * mm});
            skLineSegment(sketch, "E109", {"start": v(44.87, -14.02) * mm, "end": v(44.75, 0.4) * mm});
            skLineSegment(sketch, "E110", {"start": v(53.58, 3.45) * mm, "end": v(59.92, 2.48) * mm});
            skLineSegment(sketch, "E111", {"start": v(59.92, 2.48) * mm, "end": v(63.11, -5.84) * mm});
            skLineSegment(sketch, "E112", {"start": v(63.11, -5.84) * mm, "end": v(63.4, 1.7) * mm});
            skLineSegment(sketch, "E113", {"start": v(63.4, 1.7) * mm, "end": v(67.97, 0.77) * mm});
            skLineSegment(sketch, "E114", {"start": v(67.97, 0.77) * mm, "end": v(67.97, -22.4) * mm});
            skLineSegment(sketch, "E115", {"start": v(67.97, -22.4) * mm, "end": v(63.3, -21.3) * mm});
            skLineSegment(sketch, "E116", {"start": v(63.3, -21.3) * mm, "end": v(63.3, -16.08) * mm});
            skLineSegment(sketch, "E117", {"start": v(63.3, -16.08) * mm, "end": v(60.16, -8.27) * mm});
            skLineSegment(sketch, "E118", {"start": v(60.16, -8.27) * mm, "end": v(60.16, -20.98) * mm});
            skLineSegment(sketch, "E119", {"start": v(60.16, -20.98) * mm, "end": v(54.98, -19.97) * mm});
            skLineSegment(sketch, "E120", {"start": v(54.98, -19.97) * mm, "end": v(54.98, -0.83) * mm});
            skLineSegment(sketch, "E121", {"start": v(54.98, -0.83) * mm, "end": v(53.58, 3.45) * mm});
            skLineSegment(sketch, "E122", {"start": v(-37.2, 6.47) * mm, "end": v(-29.16, 7.2) * mm});
            skLineSegment(sketch, "E123", {"start": v(-29.16, 7.2) * mm, "end": v(-24.93, -15.66) * mm});
            skLineSegment(sketch, "E124", {"start": v(-24.93, -15.66) * mm, "end": v(-30.16, -16.06) * mm});
            skLineSegment(sketch, "E125", {"start": v(-30.16, -16.06) * mm, "end": v(-30.48, -11.91) * mm});
            skLineSegment(sketch, "E126", {"start": v(-30.48, -11.91) * mm, "end": v(-34.79, -11.91) * mm});
            skLineSegment(sketch, "E127", {"start": v(-34.79, -11.91) * mm, "end": v(-35.34, -16.67) * mm});
            skLineSegment(sketch, "E128", {"start": v(-35.34, -16.67) * mm, "end": v(-40.72, -17.27) * mm});
            skLineSegment(sketch, "E129", {"start": v(-40.72, -17.27) * mm, "end": v(-37.25, 1.96) * mm});
            skLineSegment(sketch, "E130", {"start": v(-37.25, 1.96) * mm, "end": v(-38.86, 1.56) * mm});
            skLineSegment(sketch, "E131", {"start": v(-38.86, 1.56) * mm, "end": v(-37.2, 6.47) * mm});
            skLineSegment(sketch, "E132", {"start": v(-54.13, 3.45) * mm, "end": v(-55.77, -0.51) * mm});
            skLineSegment(sketch, "E133", {"start": v(-55.77, -0.51) * mm, "end": v(-54.38, -0.51) * mm});
            skLineSegment(sketch, "E134", {"start": v(-54.38, -0.51) * mm, "end": v(-54.38, -19.21) * mm});
            skLineSegment(sketch, "E135", {"start": v(-54.38, -19.21) * mm, "end": v(-49.64, -18.34) * mm});
            skLineSegment(sketch, "E136", {"start": v(-49.64, -18.34) * mm, "end": v(-49.64, -10.05) * mm});
            skLineSegment(sketch, "E137", {"start": v(-49.64, -10.05) * mm, "end": v(-46.07, -17.94) * mm});
            skLineSegment(sketch, "E138", {"start": v(-46.07, -17.94) * mm, "end": v(-41.37, -17.07) * mm});
            skLineSegment(sketch, "E139", {"start": v(-41.37, -17.07) * mm, "end": v(-44.37, -8.95) * mm});
            skLineSegment(sketch, "E140", {"start": v(-54.13, 3.45) * mm, "end": v(-45.1, 5.07) * mm});
            skLineSegment(sketch, "E141", {"start": v(-13.7, 3.46) * mm, "end": v(-11.48, 7.8) * mm});
            skFitSpline(sketch, "E142", {"points": [v(-11.48, 7.8) * mm, v(-21.33, 7.8) * mm, v(-21.76, 7.8) * mm, v(-22.32, 7.42) * mm, v(-23.26, 6.37) * mm, v(-23.79, 5.46) * mm, v(-23.79, 5.18) * mm, v(-23.96, -13.39) * mm, v(-23.82, -13.8) * mm, v(-23.33, -14.58) * mm, v(-22.42, -15.07) * mm, v(-21.05, -15.32) * mm, v(-11.48, -14.54) * mm], "startDerivative": vector(-78.08, -0.84) * mm, "endDerivative": vector(70.7, 6.7) * mm});
            skFitSpline(sketch, "E143", {"points": [v(-45.1, 5.07) * mm, v(-43.57, 5.07) * mm, v(-42.38, 4.6) * mm, v(-41.74, 3.25) * mm, v(-41.55, -6.07) * mm, v(-41.66, -6.44) * mm, v(-42.32, -7.64) * mm, v(-43.23, -8.43) * mm, v(-44.37, -8.95) * mm], "startDerivative": vector(13.38, 1.08) * mm, "endDerivative": vector(-11.36, -4.6) * mm});
            skFitSpline(sketch, "E144", {"points": [v(1.45, 8.23) * mm, v(-7.25, 8.27) * mm, v(-7.92, 7.8) * mm, v(-8.5, 7.29) * mm, v(-8.97, 6.47) * mm, v(-9.09, 5.73) * mm, v(-9.32, -12.33) * mm, v(-9.28, -12.84) * mm, v(-8.93, -13.58) * mm, v(-8.2, -14.25) * mm, v(-7.7, -14.54) * mm, v(-6.89, -14.54) * mm, v(1.33, -14.54) * mm, v(1.89, -14.54) * mm, v(2.39, -14.25) * mm, v(3.32, -13.39) * mm, v(3.56, -12.96) * mm, v(3.64, 5.8) * mm, v(3.53, 6.47) * mm, v(3.13, 7.17) * mm, v(2.35, 7.8) * mm, v(1.45, 8.23) * mm]});
            skFitSpline(sketch, "E145", {"points": [v(38.87, 5.34) * mm, v(38.87, 5.73) * mm, v(38.42, 5.8) * mm, v(30.76, 6.47) * mm, v(30.16, 6.26) * mm, v(29.6, 5.84) * mm, v(28.69, 4.67) * mm, v(28.53, 2.79) * mm, v(28.27, -14.1) * mm, v(28.35, -14.41) * mm, v(28.6, -14.99) * mm, v(29.04, -15.47) * mm, v(29.61, -15.94) * mm, v(30.7, -16.51) * mm, v(31.93, -16.78) * mm, v(36.47, -17.13) * mm], "startDerivative": vector(1.6, 15.17) * mm, "endDerivative": vector(48.7, -5.53) * mm});
            skPoint(sketch, "E146.14.internal.snap0", {"position": v(63.3, -18.68) * mm});
            skFitSpline(sketch, "E146", {"points": [v(50.5, 4.07) * mm, v(42.5, 5.07) * mm, v(41.46, 5.07) * mm, v(40.8, 4.67) * mm, v(40.42, 4.07) * mm, v(40.1, 3.01) * mm, v(39.83, -15.3) * mm, v(39.92, -15.6) * mm, v(40.2, -16.08) * mm, v(40.63, -16.7) * mm, v(41.65, -17.48) * mm, v(43.7, -18.06) * mm, v(50.31, -19.1) * mm, v(50.92, -19) * mm, v(51.8, -18.68) * mm, v(52.42, -18.09) * mm, v(52.72, -17.13) * mm, v(52.76, -16.08) * mm, v(52.78, 1) * mm, v(52.67, 1.56) * mm, v(52.38, 2.27) * mm, v(51.93, 2.99) * mm, v(51.25, 3.62) * mm, v(50.5, 4.07) * mm]});
            skSolve(sketch);
        }
        {
            var Q0;
            Q0=qCreatedBy(makeId("Top.planeOp"),FACE);
            var sketch = newSketch(context, id + "F3", { "sketchPlane" : qUnion([Q0])});
            skCircle(sketch, "E147", {"center": v(-3.31, 16.37) * mm, "radius": 58.27 * mm});
            skCircle(sketch, "E148.0", {"center": v(-3.31, 16.37) * mm, "radius": 56.27 * mm});
            skSolve(sketch);
        }
        {
            var Q0;
            Q0=makeQuery(id+"F0.imprint","IMPRINT",FACE,{"disambiguationData":[TD([[makeQuery(id+"F0.imprint","IMPRINT",EDGE,{"derivedFrom":sQuery(id+"F0.wireOp",EDGE,"E2")}),-1.0]])]});
            var Q1;
            Q1=makeQuery(id+"F0.imprint","IMPRINT",FACE,{"disambiguationData":[TD([[makeQuery(id+"F0.imprint","IMPRINT",EDGE,{"derivedFrom":sQuery(id+"F0.wireOp",EDGE,"E21")}),-1.0]])]});
            var Q2;
            Q2=makeQuery(id+"F0.imprint","IMPRINT",FACE,{"disambiguationData":[TD([[makeQuery(id+"F0.imprint","IMPRINT",EDGE,{"derivedFrom":sQuery(id+"F0.wireOp",EDGE,"E18")}),-1.0]])]});
            extrude(context, id + "F4", {"entities" : qUnion([Q0, Q1, Q2]), "depth" : 6 * mm});
        }
        {
            var Q0;
            Q0 = qSketchRegion(id + "F1", true);
            extrude(context, id + "F5", {"entities" : qUnion([Q0]), "depth" : 9 * mm});
        }
        {
            var Q0;
            Q0 = qSketchRegion(id + "F2", true);
            extrude(context, id + "F6", {"entities" : qUnion([Q0]), "depth" : 12 * mm});
        }
        {
            var Q0;
            Q0=makeQuery(id+"F3.imprint","IMPRINT",FACE,{"disambiguationData":[TD([[makeQuery(id+"F3.imprint","IMPRINT",EDGE,{"derivedFrom":sQuery(id+"F3.wireOp",EDGE,"E148.0")}),1.0]])]});
            var Q1;
            Q1=makeQuery(id+"F3.imprint","IMPRINT",FACE,{"disambiguationData":[TD([[makeQuery(id+"F3.imprint","IMPRINT",EDGE,{"derivedFrom":sQuery(id+"F3.wireOp",EDGE,"E147")}),1.0]])]});
            extrude(context, id + "F7", {"entities" : qUnion([Q0, Q1]), "depth" : 3 * mm});
        }
    });
